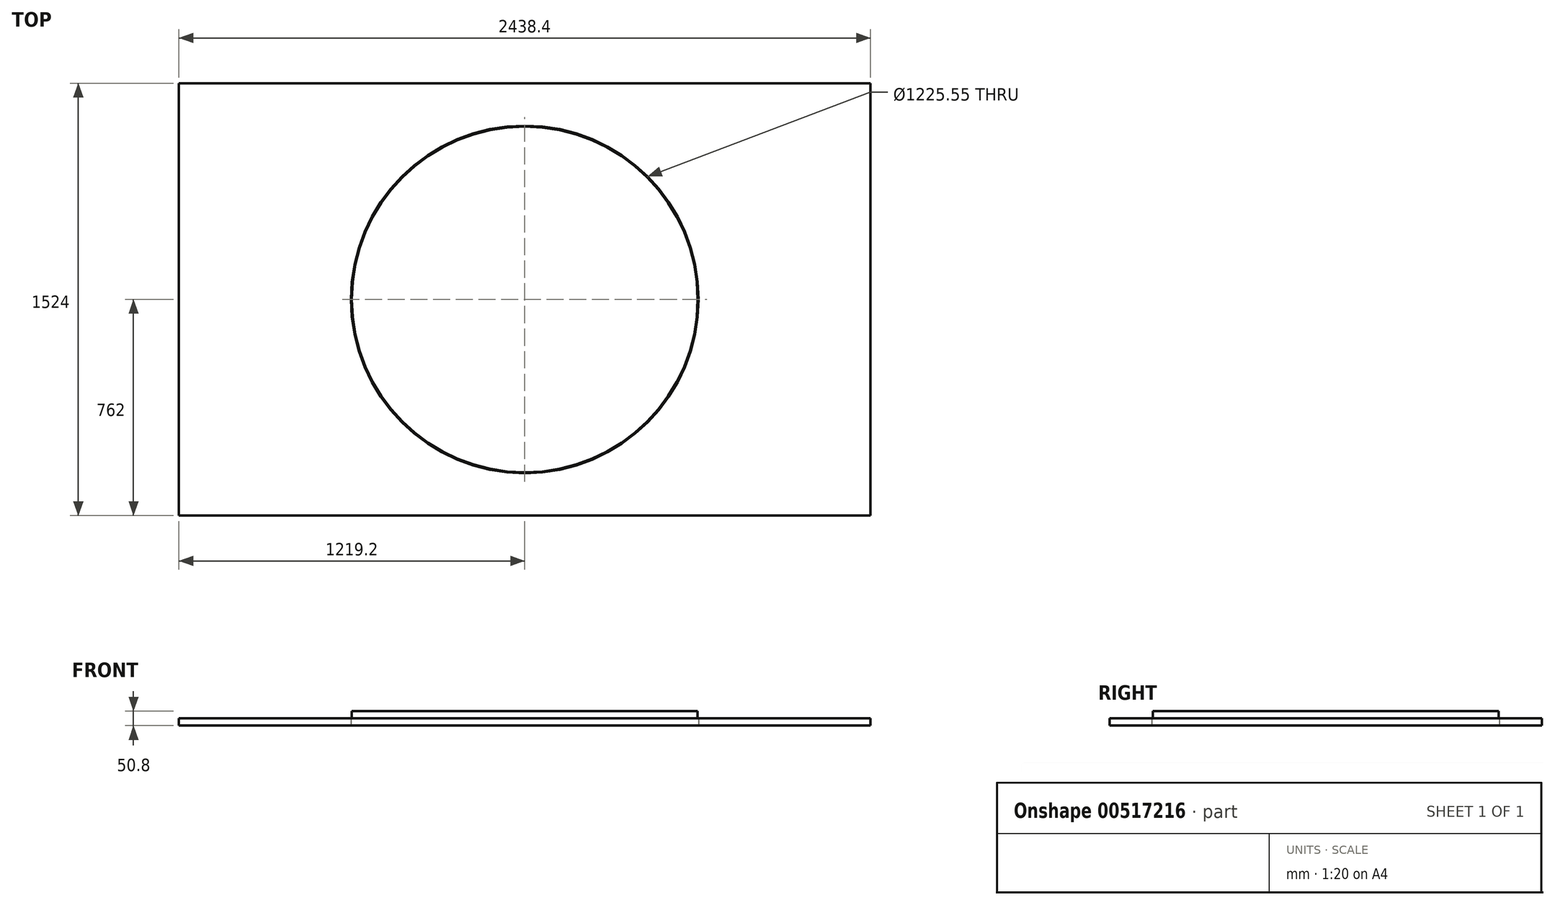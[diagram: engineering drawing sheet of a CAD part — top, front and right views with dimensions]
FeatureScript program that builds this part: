
annotation { "Feature Type Name" : "Feature", "Feature Type Description" : "" }
export const myFeature = defineFeature(function(context is Context, id is Id, definition is map)
    precondition{}
    {
        {
            var Q0;
            Q0=qCreatedBy(makeId("Top.planeOp"),FACE);
            var sketch = newSketch(context, id + "F0", { "sketchPlane" : qUnion([Q0])});
            skCircle(sketch, "E0", {"center": v(0, 0) * mm, "radius": 612.78 * mm});
            skLineSegment(sketch, "E1.bottom", {"start": v(-1219.2, 762) * mm, "end": v(1219.2, 762) * mm});
            skLineSegment(sketch, "E1.top", {"start": v(-1219.2, -762) * mm, "end": v(1219.2, -762) * mm});
            skLineSegment(sketch, "E1.left", {"start": v(-1219.2, 762) * mm, "end": v(-1219.2, -762) * mm});
            skLineSegment(sketch, "E1.right", {"start": v(1219.2, 762) * mm, "end": v(1219.2, -762) * mm});
            skSolve(sketch);
        }
        {
            var Q0;
            Q0=makeQuery(id+"F0.imprint","IMPRINT",FACE,{"disambiguationData":[TD([[makeQuery(id+"F0.imprint","IMPRINT",EDGE,{"derivedFrom":sQuery(id+"F0.wireOp",EDGE,"E0")}),-1.0]])]});
            extrude(context, id + "F1", {"entities" : qUnion([Q0]), "depth" : 25.4 * mm, "offsetDistance" : 25.4 * mm});
        }
        {
            var Q0;
            Q0=makeQuery(id+"F1.opExtrude","CAP_FACE",FACE,{"disambiguationData":[OSD([sQuery(id+"F0.wireOp",EDGE,"E0"),sQuery(id+"F0.wireOp",EDGE,"E1.bottom"),sQuery(id+"F0.wireOp",EDGE,"E1.top"),sQuery(id+"F0.wireOp",EDGE,"E1.left"),sQuery(id+"F0.wireOp",EDGE,"E1.right")])],"isStart":false});
            var sketch = newSketch(context, id + "F2", { "sketchPlane" : qUnion([Q0])});
            skCircle(sketch, "E2", {"center": v(0, 0) * mm, "radius": 609.6 * mm});
            skSolve(sketch);
        }
        {
            var Q0;
            Q0=makeQuery(id+"F2.imprint","IMPRINT",FACE,{"disambiguationData":[TD([[makeQuery(id+"F2.imprint","IMPRINT",EDGE,{"derivedFrom":sQuery(id+"F2.wireOp",EDGE,"E2")}),1.0]])]});
            extrude(context, id + "F3", {"entities" : qUnion([Q0]), "depth" : 25.4 * mm, "offsetDistance" : 25.4 * mm});
        }
    });
